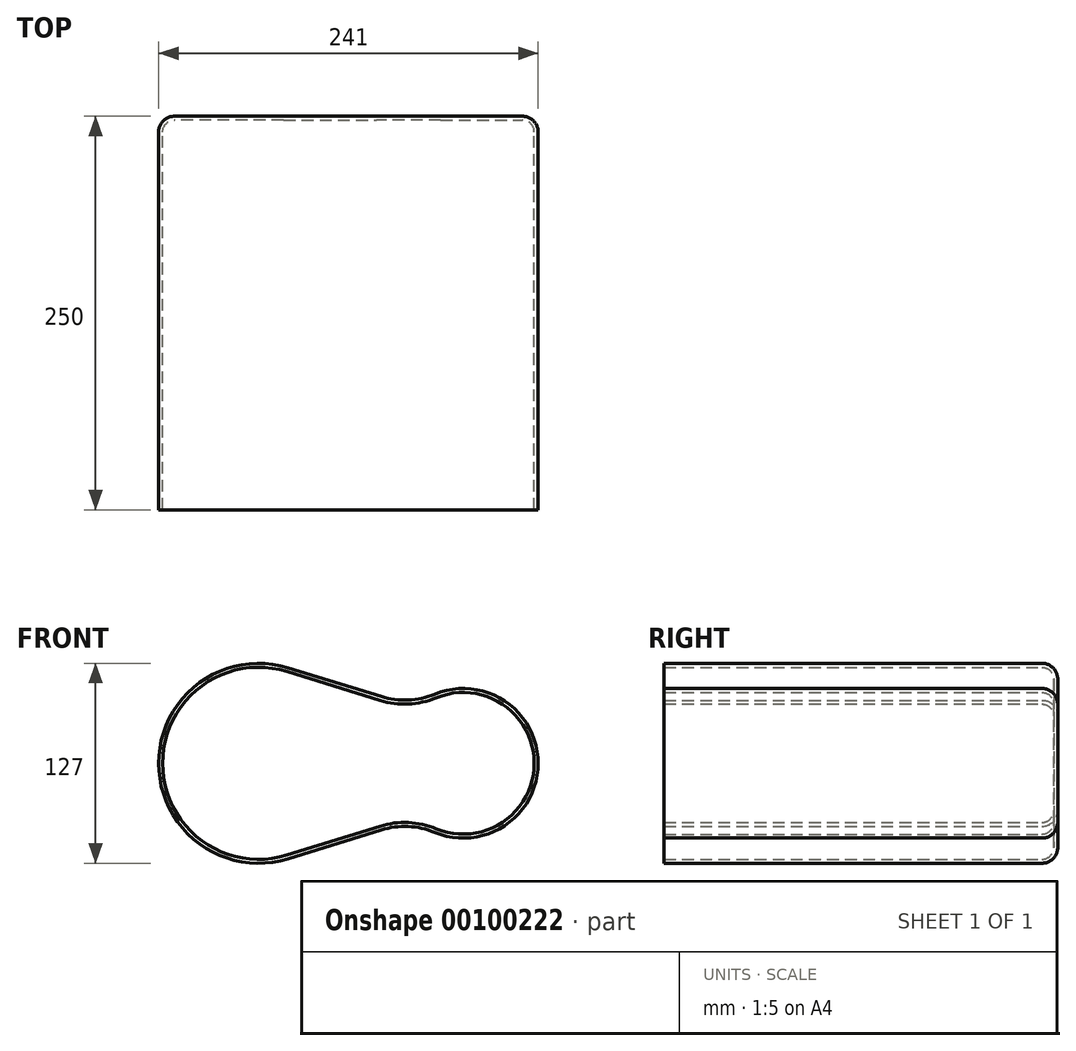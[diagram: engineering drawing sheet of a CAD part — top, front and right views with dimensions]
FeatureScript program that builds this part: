
annotation { "Feature Type Name" : "Feature", "Feature Type Description" : "" }
export const myFeature = defineFeature(function(context is Context, id is Id, definition is map)
    precondition{}
    {
        {
            var Q0;
            Q0=qCreatedBy(makeId("Front.planeOp"),FACE);
            var sketch = newSketch(context, id + "F0", { "sketchPlane" : qUnion([Q0])});
            skArc(sketch, "E0", {"start": v(18.8, 60.65) * mm, "mid": v(-63.5, 0) * mm, "end": v(18.8, -60.65) * mm});
            skArc(sketch, "E1", {"start": v(137.4, -23.88) * mm, "mid": v(155, 0) * mm, "end": v(137.4, 23.88) * mm, "construction": true});
            skLineSegment(sketch, "E2", {"start": v(18.8, 60.65) * mm, "end": v(98.83, 35.84) * mm});
            skLineSegment(sketch, "E3", {"start": v(18.8, -60.65) * mm, "end": v(98.83, -35.84) * mm});
            skArc(sketch, "E4", {"start": v(98.83, -35.84) * mm, "mid": v(177.5, 0) * mm, "end": v(98.83, 35.84) * mm});
            skSolve(sketch);
        }
        {
            var Q0;
            Q0=makeQuery(id+"F0.imprint","IMPRINT",FACE,{"disambiguationData":[TD([[makeQuery(id+"F0.imprint","IMPRINT",EDGE,{"derivedFrom":sQuery(id+"F0.wireOp",EDGE,"E0")}),1.0]])]});
            extrude(context, id + "F1", {"entities" : qUnion([Q0]), "endBound" : BoundingType.SYMMETRIC, "depth" : 250 * mm});
        }
        {
            var Q0;
            Q0=makeQuery(id+"F1.opExtrude","SWEPT_EDGE",EDGE,{"disambiguationData":[OSD([sQuery(id+"F0.wireOp",EDGE,"E2"),sQuery(id+"F0.wireOp",EDGE,"E4")])]});
            var Q1;
            Q1=makeQuery(id+"F1.opExtrude","SWEPT_EDGE",EDGE,{"disambiguationData":[OSD([sQuery(id+"F0.wireOp",EDGE,"E3"),sQuery(id+"F0.wireOp",EDGE,"E4")])]});
            fillet(context, id + "F2", {"entities" : qUnion([Q0, Q1]), "radius" : 50 * mm, "tangentPropagation" : true, "allowEdgeOverflow" : false});
        }
        {
            var Q0;
            Q0=makeQuery(id+"F1.opExtrude","CAP_EDGE",EDGE,{"disambiguationData":[OSD([sQuery(id+"F0.wireOp",EDGE,"E3")])],"isStart":true});
            fillet(context, id + "F3", {"entities" : qUnion([Q0]), "radius" : 10 * mm, "tangentPropagation" : true, "allowEdgeOverflow" : false});
        }
        {
            var Q0;
            Q0=makeQuery(id+"F1.opExtrude","CAP_FACE",FACE,{"disambiguationData":[OSD([sQuery(id+"F0.wireOp",EDGE,"E0"),sQuery(id+"F0.wireOp",EDGE,"E2"),sQuery(id+"F0.wireOp",EDGE,"E3"),sQuery(id+"F0.wireOp",EDGE,"E4")])],"isStart":false});
            shell(context, id + "F4", {"entities" : qUnion([Q0]), "thickness" : 2.5 * mm});
        }
    });
